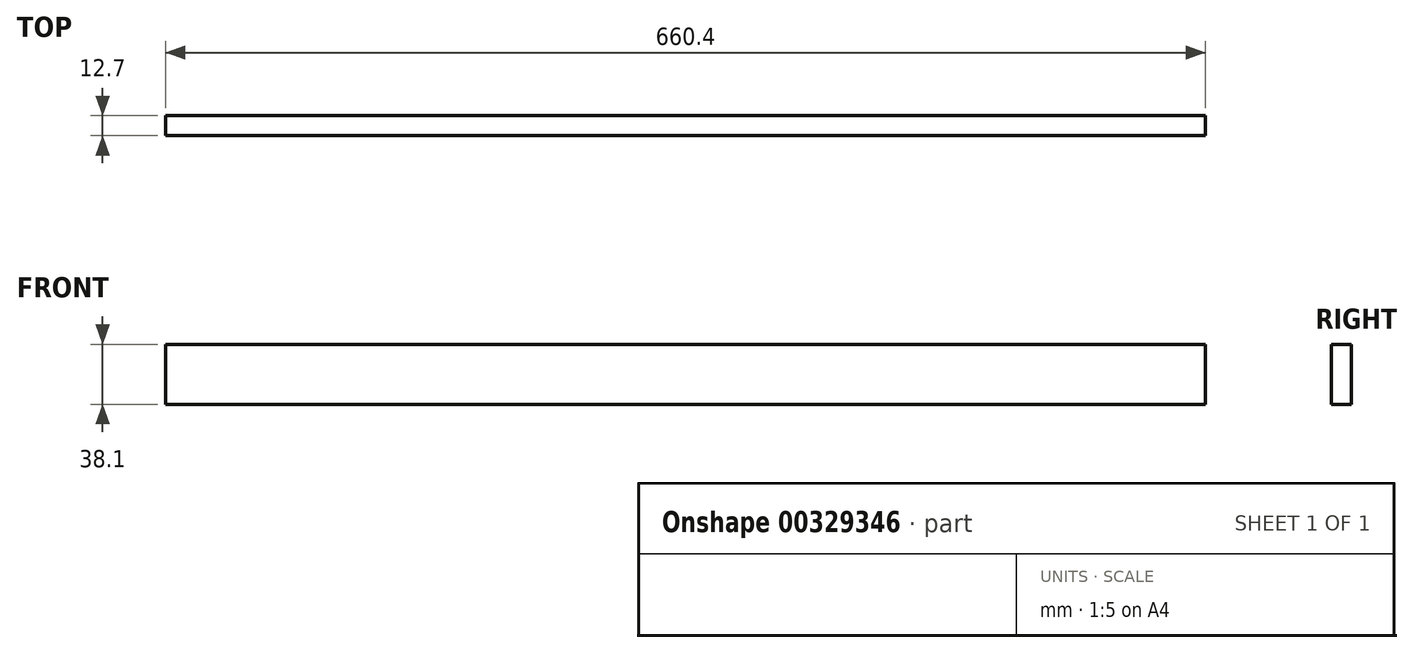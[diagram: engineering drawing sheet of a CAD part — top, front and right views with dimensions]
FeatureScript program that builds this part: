
annotation { "Feature Type Name" : "Feature", "Feature Type Description" : "" }
export const myFeature = defineFeature(function(context is Context, id is Id, definition is map)
    precondition{}
    {
        {
            var Q0;
            Q0=qCreatedBy(makeId("Right.planeOp"),FACE);
            var sketch = newSketch(context, id + "F0", { "sketchPlane" : qUnion([Q0])});
            skLineSegment(sketch, "E0.bottom", {"start": v(0, 0) * mm, "end": v(12.7, 0) * mm});
            skLineSegment(sketch, "E0.top", {"start": v(0, -38.1) * mm, "end": v(12.7, -38.1) * mm});
            skLineSegment(sketch, "E0.left", {"start": v(0, 0) * mm, "end": v(0, -38.1) * mm});
            skLineSegment(sketch, "E0.right", {"start": v(12.7, 0) * mm, "end": v(12.7, -38.1) * mm});
            skSolve(sketch);
        }
        {
            var Q0;
            Q0=makeQuery(id+"F0.imprint","IMPRINT",FACE,{"disambiguationData":[TD([[makeQuery(id+"F0.imprint","IMPRINT",EDGE,{"derivedFrom":sQuery(id+"F0.wireOp",EDGE,"E0.bottom")}),-1.0]])]});
            extrude(context, id + "F1", {"entities" : qUnion([Q0]), "depth" : 660.4 * mm});
        }
    });
